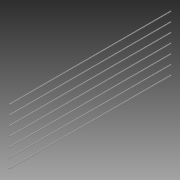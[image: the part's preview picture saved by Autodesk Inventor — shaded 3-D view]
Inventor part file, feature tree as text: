
AUTODESK INVENTOR PART (.ipt)
format: ipt  version: 2015 (Build 190159000, 159)  size: 85,504 bytes
history: native  units: in
note: dims shown in document units (in); Inventor stores cm internally (conversion verified against a paired STEP export)
features: extrude x1, sketch x1
ambient origin geometry x8: Origin, YZ Plane, XZ Plane, XY Plane, X Axis, Y Axis, Z Axis, Center Point
bodies: Body1 (feature_tree)
feature tree (2):
  extrude  "Extrusion2"  Depth=4.0in
  sketch  "Sketch1"  dims[d0=0.375in d3=4.0in d4=4.0in d5=4.0in d6=4.0in d7=4.0in d8=70.0in d9=0.0in d10=4.0in]
